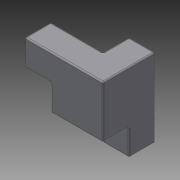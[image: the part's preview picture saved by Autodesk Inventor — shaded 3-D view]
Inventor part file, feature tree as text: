
AUTODESK INVENTOR PART (.ipt)
format: ipt  version: 2014 (Build 180170000, 170)  size: 237,056 bytes
history: native  units: in
note: dims shown in document units (in); Inventor stores cm internally (conversion verified against a paired STEP export)
features: plane x8, extrude x2, other x1, shell x1, fillet x1, sketch x1
ambient origin geometry x8: Origin, YZ Plane, XZ Plane, XY Plane, X Axis, Y Axis, Z Axis, Center Point
bodies: Solid1 (feature_tree)
feature tree (14):
  other  "Cube Master.ipt"
  extrude  "Extrusion1"  Depth=0.3937in
  extrude  "Extrusion2"  Depth=0.0193in TaperAngle=0.0deg
  shell  "Shell1"  Thickness=1.0in
  fillet  "Fillet1"  Radius=0.0394in
  sketch  "Sketch1"  dims[d0=0.3937in d1=0.3937in d2=1.0in d3=0.0in d4=1.0in d5=0.0in d6=0.0394in d7=0.0193in d8=0.0193in]
  plane  "Work Plane1"
  plane  "Work Plane2"
  plane  "Work Plane3"
  plane  "Work Plane4"
  plane  "Work Plane5"
  plane  "Work Plane6"
  plane  "Work Plane7"
  plane  "Work Plane8"
